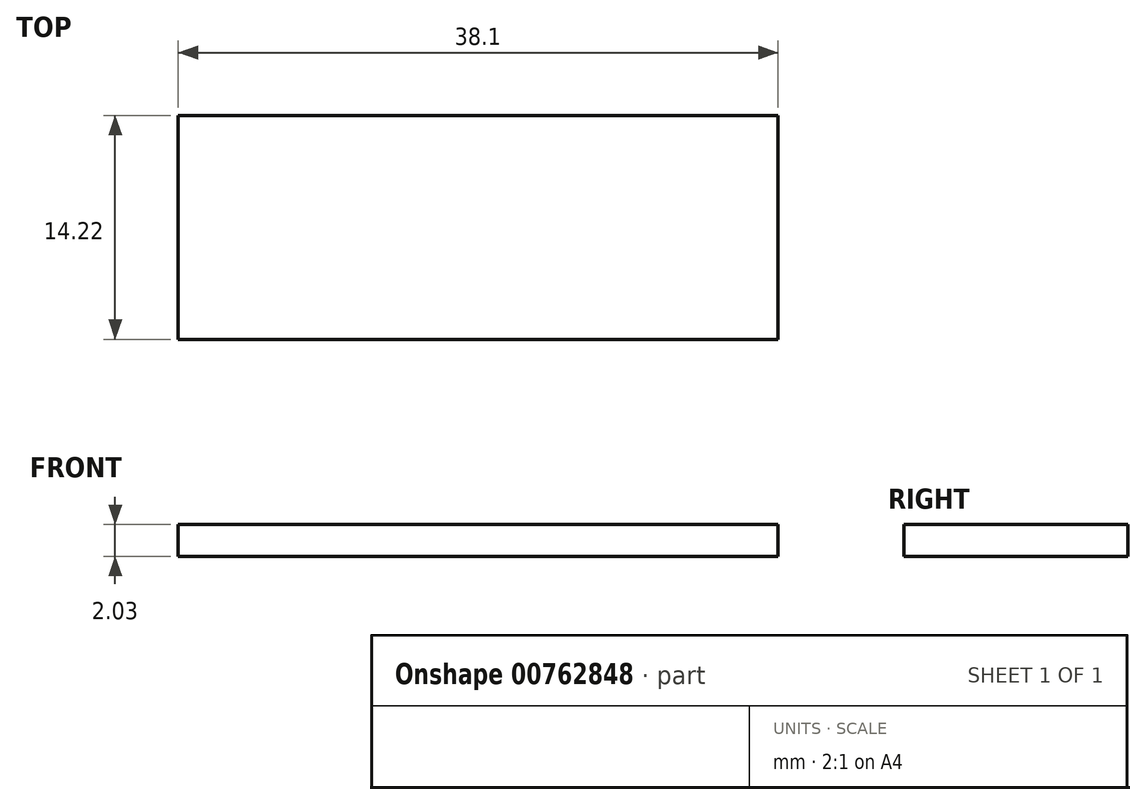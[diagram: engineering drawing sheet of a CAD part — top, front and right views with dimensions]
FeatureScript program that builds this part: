
annotation { "Feature Type Name" : "Feature", "Feature Type Description" : "" }
export const myFeature = defineFeature(function(context is Context, id is Id, definition is map)
    precondition{}
    {
        {
            var Q0;
            Q0=qCreatedBy(makeId("Top.planeOp"),FACE);
            var sketch = newSketch(context, id + "F0", { "sketchPlane" : qUnion([Q0])});
            skLineSegment(sketch, "E0.bottom", {"start": v(-19.05, 7.11) * mm, "end": v(19.05, 7.11) * mm});
            skLineSegment(sketch, "E0.top", {"start": v(-19.05, -7.11) * mm, "end": v(19.05, -7.11) * mm});
            skLineSegment(sketch, "E0.left", {"start": v(-19.05, 7.11) * mm, "end": v(-19.05, -7.11) * mm});
            skLineSegment(sketch, "E0.right", {"start": v(19.05, 7.11) * mm, "end": v(19.05, -7.11) * mm});
            skPoint(sketch, "E0.middle", {"position": v(0, 0) * mm});
            skSolve(sketch);
        }
        {
            var Q0;
            Q0 = qSketchRegion(id + "F0", true);
            extrude(context, id + "F1", {"entities" : qUnion([Q0]), "depth" : 2.03 * mm, "offsetDistance" : 25.4 * mm});
        }
    });
